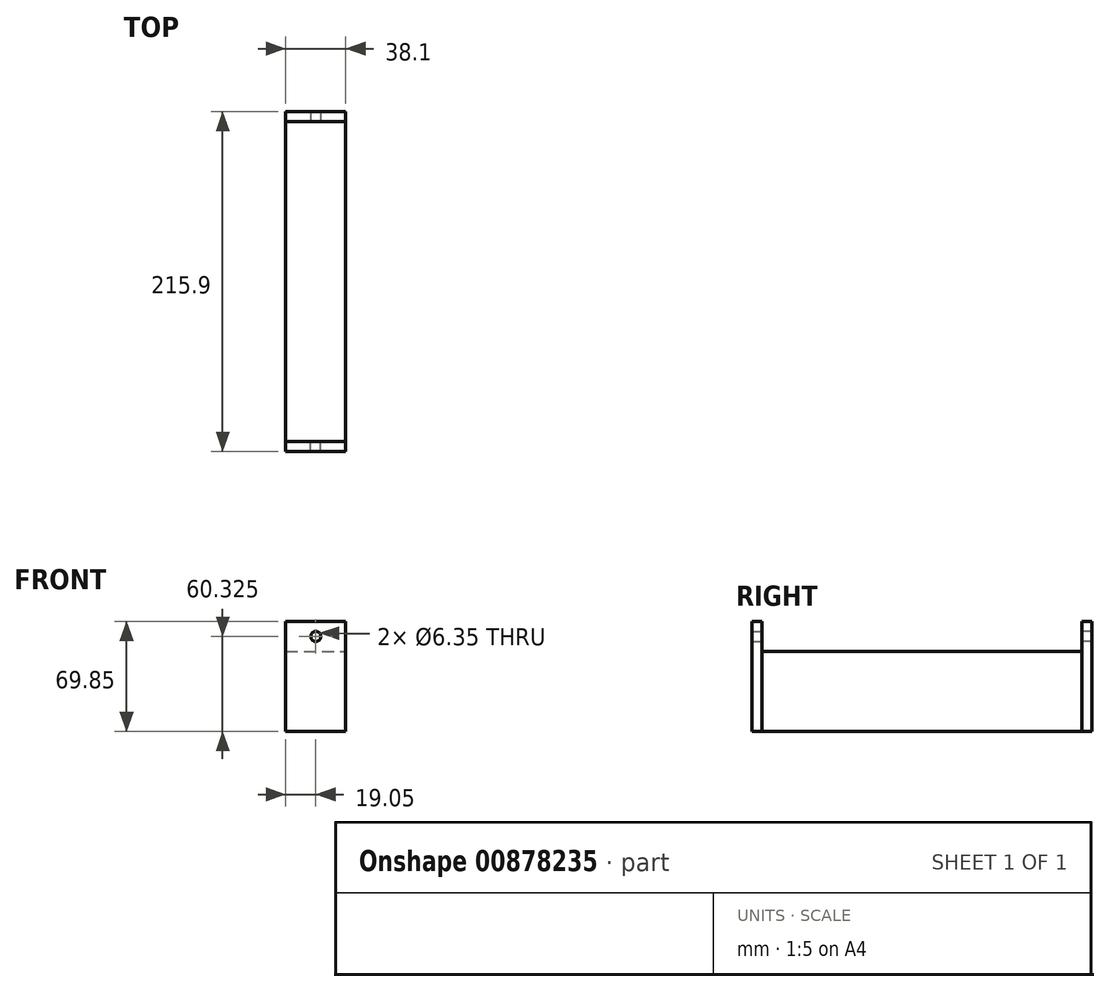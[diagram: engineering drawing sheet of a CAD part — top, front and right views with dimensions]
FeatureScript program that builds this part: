
annotation { "Feature Type Name" : "Feature", "Feature Type Description" : "" }
export const myFeature = defineFeature(function(context is Context, id is Id, definition is map)
    precondition{}
    {
        {
            var Q0;
            Q0=qCreatedBy(makeId("Front.planeOp"),FACE);
            var sketch = newSketch(context, id + "F0", { "sketchPlane" : qUnion([Q0])});
            skLineSegment(sketch, "E0.bottom", {"start": v(0, 0) * mm, "end": v(38.1, 0) * mm});
            skLineSegment(sketch, "E0.top", {"start": v(0, 50.8) * mm, "end": v(38.1, 50.8) * mm});
            skLineSegment(sketch, "E0.left", {"start": v(0, 0) * mm, "end": v(0, 50.8) * mm});
            skLineSegment(sketch, "E0.right", {"start": v(38.1, 0) * mm, "end": v(38.1, 50.8) * mm});
            skSolve(sketch);
        }
        {
            var Q0;
            Q0 = qSketchRegion(id + "F0", true);
            extrude(context, id + "F1", {"entities" : qUnion([Q0]), "depth" : 203.2 * mm, "offsetDistance" : 25.4 * mm});
        }
        {
            var Q0;
            Q0=makeQuery(id+"F1.opExtrude","SWEPT_FACE",FACE,{"disambiguationData":[OSD([sQuery(id+"F0.wireOp",EDGE,"E0.right")])]});
            var sketch = newSketch(context, id + "F2", { "sketchPlane" : qUnion([Q0])});
            skLineSegment(sketch, "E1", {"start": v(-101.6, 50.8) * mm, "end": v(-101.6, 0) * mm, "construction": true});
            skSolve(sketch);
        }
        {
            var Q0;
            Q0=makeQuery(id+"F1.opExtrude","SWEPT_EDGE",EDGE,{"disambiguationData":[OSD([sQuery(id+"F0.wireOp",EDGE,"E0.top"),sQuery(id+"F0.wireOp",EDGE,"E0.left")])]});
            cPoint(context, id + "F3", {"entities" : qUnion([Q0]), "parameter" : 0.5});
        }
        {
            var Q0;
            Q0=makeQuery(id+"F1.opExtrude","SWEPT_EDGE",EDGE,{"disambiguationData":[OSD([sQuery(id+"F0.wireOp",EDGE,"E0.bottom"),sQuery(id+"F0.wireOp",EDGE,"E0.right")])]});
            cPoint(context, id + "F4", {"entities" : qUnion([Q0]), "parameter" : 0.5});
        }
        {
            var Q0;
            Q0 = qCreatedBy(id + "F3" ,VERTEX);
            var Q1;
            Q1=sQuery(id+"F2.wireOp",VERTEX,"E1.start");
            var Q2;
            Q2 = qCreatedBy(id + "F4" ,VERTEX);
            cPlane(context, id + "F5", {"entities" : qUnion([Q0, Q1, Q2]), "cplaneType" : CPlaneType.THREE_POINT, "offset" : 25.4 * mm, "width" : 152.4 * mm, "height" : 152.4 * mm});
        }
        {
            var Q0;
            Q0=makeQuery(id+"F1.opExtrude","CAP_FACE",FACE,{"disambiguationData":[OSD([sQuery(id+"F0.wireOp",EDGE,"E0.bottom"),sQuery(id+"F0.wireOp",EDGE,"E0.top"),sQuery(id+"F0.wireOp",EDGE,"E0.left"),sQuery(id+"F0.wireOp",EDGE,"E0.right")])],"isStart":false});
            var sketch = newSketch(context, id + "F6", { "sketchPlane" : qUnion([Q0])});
            skLineSegment(sketch, "E2.bottom", {"start": v(0, 0) * mm, "end": v(38.1, 0) * mm});
            skLineSegment(sketch, "E2.top", {"start": v(0, 69.85) * mm, "end": v(38.1, 69.85) * mm});
            skLineSegment(sketch, "E2.left", {"start": v(0, 0) * mm, "end": v(0, 69.85) * mm});
            skLineSegment(sketch, "E2.right", {"start": v(38.1, 0) * mm, "end": v(38.1, 69.85) * mm});
            skCircle(sketch, "E3", {"center": v(19.05, 60.33) * mm, "radius": 3.18 * mm});
            skSolve(sketch);
        }
        {
            var Q0;
            Q0 = qSketchRegion(id + "F6", true);
            extrude(context, id + "F7", {"entities" : qUnion([Q0]), "depth" : 6.35 * mm, "offsetDistance" : 25.4 * mm});
        }
        {
            var Q0;
            Q0=makeQuery(id+"F7.opExtrude","SWEPT_BODY",BODY,{"disambiguationData":[OSD([sQuery(id+"F6.wireOp",EDGE,"E2.bottom"),sQuery(id+"F6.wireOp",EDGE,"E2.top"),sQuery(id+"F6.wireOp",EDGE,"E2.left"),sQuery(id+"F6.wireOp",EDGE,"E2.right"),sQuery(id+"F6.wireOp",EDGE,"E3")])]});
            var Q1;
            Q1=qCreatedBy(id+"F5.planeOp",FACE);
            mirror(context, id + "F8", {"entities" : qUnion([Q0]), "mirrorPlane" : qUnion([Q1])});
        }
    });
